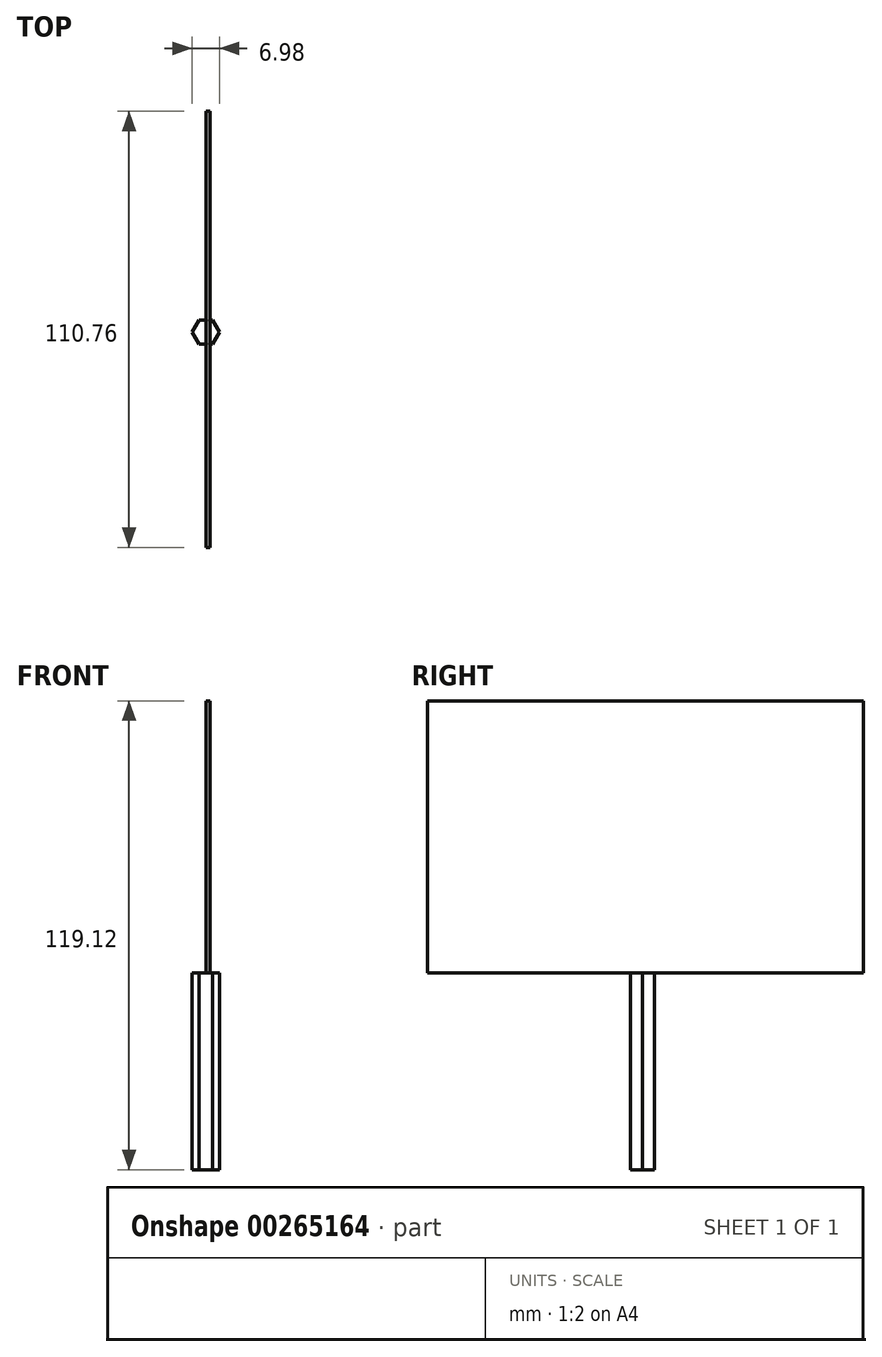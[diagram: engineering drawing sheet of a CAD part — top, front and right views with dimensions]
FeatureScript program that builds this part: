
annotation { "Feature Type Name" : "Feature", "Feature Type Description" : "" }
export const myFeature = defineFeature(function(context is Context, id is Id, definition is map)
    precondition{}
    {
        {
            var Q0;
            Q0=qCreatedBy(makeId("Right.planeOp"),FACE);
            var sketch = newSketch(context, id + "F0", { "sketchPlane" : qUnion([Q0])});
            skLineSegment(sketch, "E0.bottom", {"start": v(-54.67, 0) * mm, "end": v(56.09, 0) * mm});
            skLineSegment(sketch, "E0.top", {"start": v(-54.67, 69.12) * mm, "end": v(56.09, 69.12) * mm});
            skLineSegment(sketch, "E0.left", {"start": v(-54.67, 0) * mm, "end": v(-54.67, 69.12) * mm});
            skLineSegment(sketch, "E0.right", {"start": v(56.09, 0) * mm, "end": v(56.09, 69.12) * mm});
            skLineSegment(sketch, "E1.bottom", {"start": v(-8.21, 0) * mm, "end": v(6.52, 0) * mm});
            skSolve(sketch);
        }
        {
            var Q0;
            Q0=qCreatedBy(makeId("Top.planeOp"),FACE);
            var sketch = newSketch(context, id + "F1", { "sketchPlane" : qUnion([Q0])});
            skCircle(sketch, "E2.cCircle", {"center": v(0, 0) * mm, "radius": 3.02 * mm, "construction": true});
            skLineSegment(sketch, "E2.0", {"start": v(-1.75, 3.02) * mm, "end": v(1.75, 3.02) * mm});
            skLineSegment(sketch, "E2.1", {"start": v(1.75, 3.02) * mm, "end": v(3.5, 0) * mm});
            skLineSegment(sketch, "E2.2", {"start": v(3.5, 0) * mm, "end": v(1.75, -3.02) * mm});
            skLineSegment(sketch, "E2.3", {"start": v(1.75, -3.02) * mm, "end": v(-1.75, -3.02) * mm});
            skLineSegment(sketch, "E2.4", {"start": v(-1.75, -3.02) * mm, "end": v(-3.5, 0) * mm});
            skLineSegment(sketch, "E2.5", {"start": v(-3.5, 0) * mm, "end": v(-1.75, 3.02) * mm});
            skPoint(sketch, "E2.0.midPoint", {"position": v(0, 3.02) * mm});
            skSolve(sketch);
        }
        {
            var Q0;
            Q0 = qSketchRegion(id + "F1", true);
            extrude(context, id + "F2", {"entities" : qUnion([Q0]), "oppositeDirection" : true, "depth" : 50 * mm});
        }
        {
            var Q0;
            Q0 = qSketchRegion(id + "F0", true);
            extrude(context, id + "F3", {"entities" : qUnion([Q0]), "operationType" : NewBodyOperationType.ADD, "depth" : 1 * mm});
        }
    });
